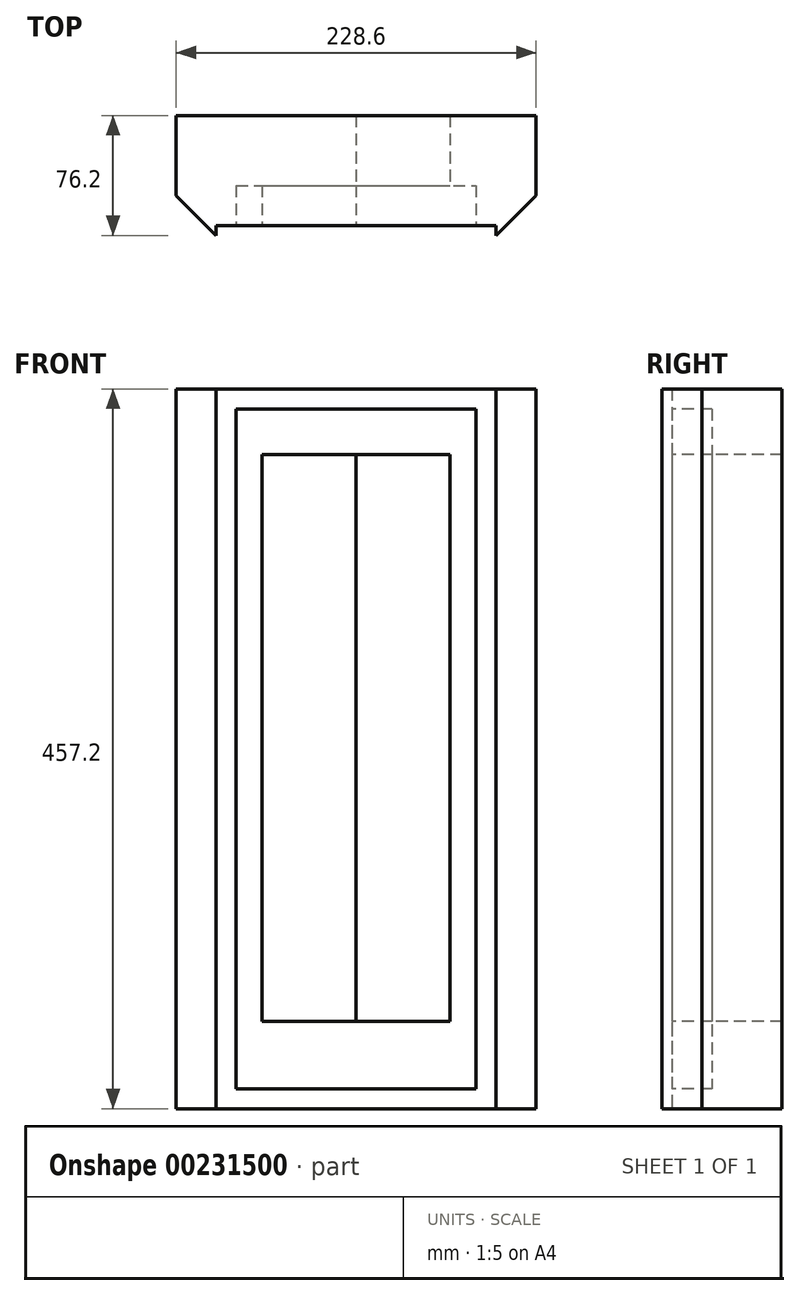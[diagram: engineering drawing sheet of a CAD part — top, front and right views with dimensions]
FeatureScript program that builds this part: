
annotation { "Feature Type Name" : "Feature", "Feature Type Description" : "" }
export const myFeature = defineFeature(function(context is Context, id is Id, definition is map)
    precondition{}
    {
        {
            var Q0;
            Q0=qCreatedBy(makeId("Top.planeOp"),FACE);
            var sketch = newSketch(context, id + "F0", { "sketchPlane" : qUnion([Q0])});
            skLineSegment(sketch, "E0.bottom", {"start": v(114.3, 38.1) * mm, "end": v(-114.3, 38.1) * mm});
            skLineSegment(sketch, "E0.top", {"start": v(114.3, -38.1) * mm, "end": v(-114.3, -38.1) * mm});
            skLineSegment(sketch, "E0.left", {"start": v(114.3, 38.1) * mm, "end": v(114.3, -38.1) * mm});
            skLineSegment(sketch, "E0.right", {"start": v(-114.3, 38.1) * mm, "end": v(-114.3, -38.1) * mm});
            skPoint(sketch, "E0.middle", {"position": v(0, 0) * mm});
            skSolve(sketch);
        }
        {
            var Q0;
            Q0=makeQuery(id+"F0.imprint","IMPRINT",FACE,{"disambiguationData":[TD([[makeQuery(id+"F0.imprint","IMPRINT",EDGE,{"derivedFrom":sQuery(id+"F0.wireOp",EDGE,"E0.bottom")}),1.0]])]});
            extrude(context, id + "F1", {"entities" : qUnion([Q0]), "depth" : 457.2 * mm});
        }
        {
            var Q0;
            Q0=makeQuery(id+"F1.opExtrude","SWEPT_EDGE",EDGE,{"disambiguationData":[OSD([sQuery(id+"F0.wireOp",EDGE,"E0.top"),sQuery(id+"F0.wireOp",EDGE,"E0.right")])]});
            var Q1;
            Q1=makeQuery(id+"F1.opExtrude","SWEPT_EDGE",EDGE,{"disambiguationData":[OSD([sQuery(id+"F0.wireOp",EDGE,"E0.top"),sQuery(id+"F0.wireOp",EDGE,"E0.left")])]});
            chamfer(context, id + "F2", {"entities" : qUnion([Q0, Q1]), "width" : 25.4 * mm, "tangentPropagation" : true});
        }
        {
            var Q0;
            Q0=makeQuery(id+"F1.opExtrude","SWEPT_FACE",FACE,{"disambiguationData":[OSD([sQuery(id+"F0.wireOp",EDGE,"E0.top")])]});
            var sketch = newSketch(context, id + "F3", { "sketchPlane" : qUnion([Q0])});
            skLineSegment(sketch, "E1", {"start": v(0, 0) * mm, "end": v(0, 457.2) * mm});
            skLineSegment(sketch, "E2.bottom", {"start": v(0, 444.5) * mm, "end": v(76.2, 444.5) * mm});
            skLineSegment(sketch, "E2.top", {"start": v(0, 12.7) * mm, "end": v(76.2, 12.7) * mm});
            skLineSegment(sketch, "E2.left", {"start": v(0, 444.5) * mm, "end": v(0, 12.7) * mm});
            skLineSegment(sketch, "E2.right", {"start": v(76.2, 444.5) * mm, "end": v(76.2, 12.7) * mm});
            skLineSegment(sketch, "E3.MirrorCS", {"start": v(-76.2, 444.5) * mm, "end": v(-76.2, 12.7) * mm});
            skLineSegment(sketch, "E4.MirrorCS", {"start": v(0, 444.5) * mm, "end": v(-76.2, 444.5) * mm});
            skLineSegment(sketch, "E5.MirrorCS", {"start": v(0, 12.7) * mm, "end": v(-76.2, 12.7) * mm});
            skLineSegment(sketch, "E6.bottom", {"start": v(0, 415.54) * mm, "end": v(59.7, 415.54) * mm});
            skLineSegment(sketch, "E6.top", {"start": v(0, 55.54) * mm, "end": v(59.7, 55.54) * mm});
            skLineSegment(sketch, "E6.left", {"start": v(0, 415.54) * mm, "end": v(0, 55.54) * mm});
            skLineSegment(sketch, "E6.right", {"start": v(59.7, 415.54) * mm, "end": v(59.7, 55.54) * mm});
            skLineSegment(sketch, "E7.MirrorCS", {"start": v(0, 415.54) * mm, "end": v(-59.7, 415.54) * mm});
            skLineSegment(sketch, "E8.MirrorCS", {"start": v(-59.7, 415.54) * mm, "end": v(-59.7, 55.54) * mm});
            skLineSegment(sketch, "E9.MirrorCS", {"start": v(0, 55.54) * mm, "end": v(-59.7, 55.54) * mm});
            skSolve(sketch);
        }
        {
            var Q0;
            Q0=makeQuery(id+"F3.imprint","IMPRINT",FACE,{"disambiguationData":[TD([[makeQuery(id+"F3.imprint","IMPRINT",EDGE,{"derivedFrom":sQuery(id+"F3.wireOp",EDGE,"E6.bottom")}),-1.0]])]});
            var Q1;
            Q1=makeQuery(id+"F3.imprint","IMPRINT",FACE,{"disambiguationData":[TD([[makeQuery(id+"F3.imprint","IMPRINT",EDGE,{"derivedFrom":sQuery(id+"F3.wireOp",EDGE,"E6.left")}),-1.0]])]});
            extrude(context, id + "F4", {"entities" : qUnion([Q0, Q1]), "operationType" : NewBodyOperationType.REMOVE, "oppositeDirection" : true, "depth" : 76.2 * mm});
        }
        {
            var Q0;
            Q0 = qSketchRegion(id + "F3", true);
            var Q1;
            Q1=makeQuery(id+"F1.opExtrude","SWEPT_FACE",FACE,{"disambiguationData":[OSD([sQuery(id+"F0.wireOp",EDGE,"E0.top")])]});
            extrude(context, id + "F5", {"entities" : qUnion([Q0, Q1]), "operationType" : NewBodyOperationType.REMOVE, "oppositeDirection" : true, "depth" : 6.35 * mm});
        }
        {
            var Q0;
            {var subQ1=sQuery(id+"F3.wireOp",EDGE,"E2.bottom");Q0=makeQuery(id+"F3.imprint","IMPRINT",FACE,{"disambiguationData":[TD([[makeQuery(id+"F3.imprint","IMPRINT",EDGE,{"derivedFrom":subQ1}),-1.0]])]});}
            var Q1;
            Q1=makeQuery(id+"F3.imprint","IMPRINT",FACE,{"disambiguationData":[TD([[makeQuery(id+"F3.imprint","IMPRINT",EDGE,{"derivedFrom":sQuery(id+"F3.wireOp",EDGE,"E3.MirrorCS")}),1.0]])]});
            extrude(context, id + "F6", {"entities" : qUnion([Q0, Q1]), "operationType" : NewBodyOperationType.REMOVE, "oppositeDirection" : true, "depth" : 31.75 * mm});
        }
    });
